# Revit family: HARMANN-SENSOVENT ROOF V EC-Wywiewny
name_source: partatom
category: Wyposażenie mechaniczne
units: mm (PartAtom-declared; Revit-internal decimal feet)

## family parameters
Oparty na płaszczyźnie roboczej = Nie
Punkt obliczania pomieszczeń = Nie
Tnij formami wycięć po wczytaniu = Nie
Typ części = Normalny
Współdzielony = Nie
Wymiar okrągłego złącza = Użyj średnicy
Zachowaj orientację opisów = Nie
Zawsze pionowo = Tak

## types (7) — shared parameters
Domyślna rzędna = 0.0 mm
IfcExportAs = IfcFanType
IfcExportType = NOTDEFINED
Kod Producent = Harmann
Kod Typoszereg = SENSOVENT ROOF V EC
Object Date = 2018.11.30
Object Destination = PL
Object ID = F000104RFAPL
Object Language = PL
Object Revit = 2017
Object Version = 1.00
Opis = Wentylator dachowy
Opt Akcesorium Podstawa A = ᴬ : Brak Podstawy
Opt Akcesorium Podstawa B = ᴬ : Podstawa Dachowa
Opt Akcesorium Podstawa C = ᴬ : Tłumiąca Podstawa Dachowa
Producent = Harmann Polska Sp. z o.o.
Producent Nazwa = Harmann Polska Sp. z o.o.
Systematyka Branża = Instalacje Sanitarne
Systematyka Dziedzina = Instalacje Wentylacyjne
Systematyka Klasa = Wentylator
Systematyka Rodzaj = Wentylator Dachowy
Zasilanie Częstotliwość Nominalna = 50 Hz
Zasilanie Ilość Faz = 1
Zasilanie Konfiguracja Uzwojeń = n/d
Zasilanie Napięcie Nominalne = 230 V
Zasilanie Rodzaj Sterowania = Sterowanie napięciem 0-10V
l1_a0 = 0.0 mm
l1_a1 = 0.0 mm
l1_a2 = 0.0 mm
l1_a3 = 0.0 mm
l1_a4 = 0.0 mm
l1_a5 = 320.0 mm
l1_a6 = 620.0 mm
l2_a0 = 0.0 mm
l2_a1 = 1.0 mm
l2_a4 = 1.0 mm
l2_a5 = 0.0 mm
l2_a6 = 0.0 mm
wz_a0 = 0.0 mm

## per-type parameters (varying)
- SENSOVENT ROOF V190 EC: Kod Numer Katalogowy=05002052; Masa Netto=4.5 kg; Opis indeksowy=SENSOVENT ROOF V190 EC; Otoczenie Poziom Ciśnienia Akustycznego Nominalny z 01 m=50; Otoczenie Poziom Ciśnienia Akustycznego Nominalny z 04 m=38; Otoczenie Poziom Ciśnienia Akustycznego Nominalny z 10 m=30; Otoczenie Poziom Mocy Akustycznej Nominalny Obudowa=61; Otoczenie Temperatura Maksymalna=60.0 °C; Otoczenie Temperatura Minimalna=-30.0 °C; Powietrze Wywiewane Ciśnienie Statyczne Maksymalne=670.0 Pa; Powietrze Wywiewane Ciśnienie Statyczne Nominalne=100.0 Pa; Powietrze Wywiewane Poziom Mocy Akustycznej Nominalny Wlot=60; Powietrze Wywiewane Przepływ Maksymalny=610 m³/h; Powietrze Wywiewane Przepływ Nominalny=250 m³/h; Powietrze Wywiewane Temperatura Maksymalna=60.0 °C; Prt Komponent A1=VE-Zagnieżdżone-Akcesorium-ParaForma-Harmann-DAF-Króciec_Przyłączeniowy : DAF 180; Prt Komponent A2=VE-Zagnieżdżone-Akcesorium-ParaForma-Harmann-DAS-Złącze_Przeciwdrganiowe : 180; Prt Komponent A3=VE-Zagnieżdżone-Akcesorium-ParaForma-Harmann-DVK-Przepustnica_Zwrotna : 180; Prt Komponent A4=VE-Zagnieżdżone-Akcesorium-ParaForma-Harmann-DKP-Płyta_Adaptacyjna : 220; Prt Komponent A5=VE-Zagnieżdżone-Akcesorium-ParaForma-Harmann-DSF_AL-Podstawa_Dachowa : 220; Prt Komponent A6=VE-Zagnieżdżone-Akcesorium-ParaForma-Harmann-DSS_AL-Podstawa_Dachowa : 220; Prt Komponent N1=GE-Komponent-ParaForma-Harmann-VIVER_EC-N1a : 2-190/600EC; Zasilanie Moc=114 W; Zasilanie Moc Pozorna=191 VA; Zasilanie Natężenie=1 A; Zasilanie Współczynnik Mocy=0.519; dn=180.0 mm; ds=220.0 mm; l2_a2=155.0 mm; l2_a3=115.0 mm; s1=180.0 mm; wx_a0=95.5 mm; wy_a0=95.5 mm
- SENSOVENT ROOF V220 EC: Kod Numer Katalogowy=05002053
05002053; Masa Netto=4.9 kg; Opis indeksowy=SENSOVENT ROOF V220 EC; Otoczenie Poziom Ciśnienia Akustycznego Nominalny z 01 m=45; Otoczenie Poziom Ciśnienia Akustycznego Nominalny z 04 m=33; Otoczenie Poziom Ciśnienia Akustycznego Nominalny z 10 m=25; Otoczenie Poziom Mocy Akustycznej Nominalny Obudowa=56; Otoczenie Temperatura Maksymalna=60.0 °C; Otoczenie Temperatura Minimalna=-30.0 °C; Powietrze Wywiewane Ciśnienie Statyczne Maksymalne=570.0 Pa; Powietrze Wywiewane Ciśnienie Statyczne Nominalne=100.0 Pa; Powietrze Wywiewane Poziom Mocy Akustycznej Nominalny Wlot=55; Powietrze Wywiewane Przepływ Maksymalny=940 m³/h; Powietrze Wywiewane Przepływ Nominalny=350 m³/h; Powietrze Wywiewane Temperatura Maksymalna=60.0 °C; Prt Komponent A1=VE-Zagnieżdżone-Akcesorium-ParaForma-Harmann-DAF-Króciec_Przyłączeniowy : DAF 180; Prt Komponent A2=VE-Zagnieżdżone-Akcesorium-ParaForma-Harmann-DAS-Złącze_Przeciwdrganiowe : 180; Prt Komponent A3=VE-Zagnieżdżone-Akcesorium-ParaForma-Harmann-DVK-Przepustnica_Zwrotna : 180; Prt Komponent A4=VE-Zagnieżdżone-Akcesorium-ParaForma-Harmann-DKP-Płyta_Adaptacyjna : 220; Prt Komponent A5=VE-Zagnieżdżone-Akcesorium-ParaForma-Harmann-DSF_AL-Podstawa_Dachowa : 220; Prt Komponent A6=VE-Zagnieżdżone-Akcesorium-ParaForma-Harmann-DSS_AL-Podstawa_Dachowa : 220; Prt Komponent N1=GE-Komponent-ParaForma-Harmann-VIVER_EC-N1a : 2-220/950EC; Zasilanie Moc=113 W; Zasilanie Moc Pozorna=214 VA; Zasilanie Natężenie=1 A; Zasilanie Współczynnik Mocy=0.528; dn=180.0 mm; ds=220.0 mm; l2_a2=155.0 mm; l2_a3=115.0 mm; s1=180.0 mm; wx_a0=95.5 mm; wy_a0=95.5 mm
- SENSOVENT ROOF V250 EC: Kod Numer Katalogowy=05002054; Masa Netto=6.5 kg; Object URL=http://www.paraforma.pl; Opis indeksowy=SENSOVENT ROOF V250 EC; Otoczenie Poziom Ciśnienia Akustycznego Nominalny z 01 m=50; Otoczenie Poziom Ciśnienia Akustycznego Nominalny z 04 m=38; Otoczenie Poziom Ciśnienia Akustycznego Nominalny z 10 m=30; Otoczenie Poziom Mocy Akustycznej Nominalny Obudowa=61; Otoczenie Temperatura Maksymalna=70.0 °C; Otoczenie Temperatura Minimalna=-30.0 °C; Powietrze Wywiewane Ciśnienie Statyczne Maksymalne=570.0 Pa; Powietrze Wywiewane Ciśnienie Statyczne Nominalne=100.0 Pa; Powietrze Wywiewane Poziom Mocy Akustycznej Nominalny Wlot=59; Powietrze Wywiewane Przepływ Maksymalny=1200 m³/h; Powietrze Wywiewane Przepływ Nominalny=450 m³/h; Powietrze Wywiewane Temperatura Maksymalna=70.0 °C; Prt Komponent A1=VE-Zagnieżdżone-Akcesorium-ParaForma-Harmann-DAF-Króciec_Przyłączeniowy : DAF 180; Prt Komponent A2=VE-Zagnieżdżone-Akcesorium-ParaForma-Harmann-DAS-Złącze_Przeciwdrganiowe : 180; Prt Komponent A3=VE-Zagnieżdżone-Akcesorium-ParaForma-Harmann-DVK-Przepustnica_Zwrotna : 180; Prt Komponent A4=VE-Zagnieżdżone-Akcesorium-ParaForma-Harmann-DKP-Płyta_Adaptacyjna : 220; Prt Komponent A5=VE-Zagnieżdżone-Akcesorium-ParaForma-Harmann-DSF_AL-Podstawa_Dachowa : 220; Prt Komponent A6=VE-Zagnieżdżone-Akcesorium-ParaForma-Harmann-DSS_AL-Podstawa_Dachowa : 220; Prt Komponent N1=GE-Komponent-ParaForma-Harmann-VIVER_EC-N1a : 2-250/1200EC; Zasilanie Moc=179 W; Zasilanie Moc Pozorna=345 VA; Zasilanie Natężenie=2 A; Zasilanie Współczynnik Mocy=0.519; dn=180.0 mm; ds=220.0 mm; l2_a2=155.0 mm; l2_a3=115.0 mm; s1=180.0 mm; wx_a0=95.5 mm; wy_a0=95.5 mm
- SENSOVENT ROOF V280 EC: Kod Numer Katalogowy=05002055; Masa Netto=8.0 kg; Opis indeksowy=SENSOVENT ROOF V280 EC; Otoczenie Poziom Ciśnienia Akustycznego Nominalny z 01 m=51; Otoczenie Poziom Ciśnienia Akustycznego Nominalny z 04 m=38; Otoczenie Poziom Ciśnienia Akustycznego Nominalny z 10 m=31; Otoczenie Poziom Mocy Akustycznej Nominalny Obudowa=62; Otoczenie Temperatura Maksymalna=55.0 °C; Otoczenie Temperatura Minimalna=-30.0 °C; Powietrze Wywiewane Ciśnienie Statyczne Maksymalne=830.0 Pa; Powietrze Wywiewane Ciśnienie Statyczne Nominalne=100.0 Pa; Powietrze Wywiewane Poziom Mocy Akustycznej Nominalny Wlot=62; Powietrze Wywiewane Przepływ Maksymalny=1970 m³/h; Powietrze Wywiewane Przepływ Nominalny=700 m³/h; Powietrze Wywiewane Temperatura Maksymalna=55.0 °C; Prt Komponent A1=VE-Zagnieżdżone-Akcesorium-ParaForma-Harmann-DAF-Króciec_Przyłączeniowy : DAF 250; Prt Komponent A2=VE-Zagnieżdżone-Akcesorium-ParaForma-Harmann-DAS-Złącze_Przeciwdrganiowe : 250; Prt Komponent A3=VE-Zagnieżdżone-Akcesorium-ParaForma-Harmann-DVK-Przepustnica_Zwrotna : 250; Prt Komponent A4=VE-Zagnieżdżone-Akcesorium-ParaForma-Harmann-DKP-Płyta_Adaptacyjna : 280; Prt Komponent A5=VE-Zagnieżdżone-Akcesorium-ParaForma-Harmann-DSF_AL-Podstawa_Dachowa : 280; Prt Komponent A6=VE-Zagnieżdżone-Akcesorium-ParaForma-Harmann-DSS_AL-Podstawa_Dachowa : 280; Prt Komponent N1=GE-Komponent-ParaForma-Harmann-VIVER_EC-N1a : 2-280/1900EC; Zasilanie Moc=268 W; Zasilanie Moc Pozorna=432 VA; Zasilanie Natężenie=2 A; Zasilanie Współczynnik Mocy=0.62; dn=250.0 mm; ds=280.0 mm; l2_a2=157.0 mm; l2_a3=156.0 mm; s1=250.0 mm; wx_a0=135.0 mm; wy_a0=135.0 mm
- SENSOVENT ROOF V350 EC: Kod Numer Katalogowy=05002056; Masa Netto=14.7 kg; Opis indeksowy=SENSOVENT ROOF V350 EC; Otoczenie Poziom Ciśnienia Akustycznego Nominalny z 01 m=46; Otoczenie Poziom Ciśnienia Akustycznego Nominalny z 04 m=34; Otoczenie Poziom Ciśnienia Akustycznego Nominalny z 10 m=26; Otoczenie Poziom Mocy Akustycznej Nominalny Obudowa=57; Otoczenie Temperatura Maksymalna=60.0 °C; Otoczenie Temperatura Minimalna=-25.0 °C; Powietrze Wywiewane Ciśnienie Statyczne Maksymalne=450.0 Pa; Powietrze Wywiewane Ciśnienie Statyczne Nominalne=100.0 Pa; Powietrze Wywiewane Poziom Mocy Akustycznej Nominalny Wlot=56; Powietrze Wywiewane Przepływ Maksymalny=2750 m³/h; Powietrze Wywiewane Przepływ Nominalny=1000 m³/h; Powietrze Wywiewane Temperatura Maksymalna=60.0 °C; Prt Komponent A1=VE-Zagnieżdżone-Akcesorium-ParaForma-Harmann-DAF-Króciec_Przyłączeniowy : DAF 400; Prt Komponent A2=VE-Zagnieżdżone-Akcesorium-ParaForma-Harmann-DAS-Złącze_Przeciwdrganiowe : 400; Prt Komponent A3=VE-Zagnieżdżone-Akcesorium-ParaForma-Harmann-DVK-Przepustnica_Zwrotna : 400; Prt Komponent A4=VE-Zagnieżdżone-Akcesorium-ParaForma-Harmann-DKP-Płyta_Adaptacyjna : 355; Prt Komponent A5=VE-Zagnieżdżone-Akcesorium-ParaForma-Harmann-DSF_AL-Podstawa_Dachowa : 355; Prt Komponent A6=VE-Zagnieżdżone-Akcesorium-ParaForma-Harmann-DSS_AL-Podstawa_Dachowa : 355; Prt Komponent N1=GE-Komponent-ParaForma-Harmann-VIVER_EC-N1a : 4-355/2700EC; Zasilanie Moc=165 W; Zasilanie Moc Pozorna=322 VA; Zasilanie Natężenie=1 A; Zasilanie Współczynnik Mocy=0.512; dn=400.0 mm; ds=355.0 mm; l2_a2=155.0 mm; l2_a3=220.0 mm; s1=400.0 mm; wx_a0=192.3 mm; wy_a0=192.5 mm
- SENSOVENT ROOF V400 EC: Kod Numer Katalogowy=05002057; Masa Netto=18.8 kg; Opis indeksowy=SENSOVENT ROOF V400 EC; Otoczenie Poziom Ciśnienia Akustycznego Nominalny z 01 m=48; Otoczenie Poziom Ciśnienia Akustycznego Nominalny z 04 m=36; Otoczenie Poziom Ciśnienia Akustycznego Nominalny z 10 m=28; Otoczenie Poziom Mocy Akustycznej Nominalny Obudowa=59; Otoczenie Temperatura Maksymalna=50.0 °C; Otoczenie Temperatura Minimalna=-25.0 °C; Powietrze Wywiewane Ciśnienie Statyczne Maksymalne=920.0 Pa; Powietrze Wywiewane Ciśnienie Statyczne Nominalne=150.0 Pa; Powietrze Wywiewane Poziom Mocy Akustycznej Nominalny Wlot=56; Powietrze Wywiewane Przepływ Maksymalny=4460 m³/h; Powietrze Wywiewane Przepływ Nominalny=1500 m³/h; Powietrze Wywiewane Temperatura Maksymalna=50.0 °C; Prt Komponent A1=VE-Zagnieżdżone-Akcesorium-ParaForma-Harmann-DAF-Króciec_Przyłączeniowy : DAF 400; Prt Komponent A2=VE-Zagnieżdżone-Akcesorium-ParaForma-Harmann-DAS-Złącze_Przeciwdrganiowe : 400; Prt Komponent A3=VE-Zagnieżdżone-Akcesorium-ParaForma-Harmann-DVK-Przepustnica_Zwrotna : 400; Prt Komponent A4=VE-Zagnieżdżone-Akcesorium-ParaForma-Harmann-DKP-Płyta_Adaptacyjna : 355; Prt Komponent A5=VE-Zagnieżdżone-Akcesorium-ParaForma-Harmann-DSF_AL-Podstawa_Dachowa : 355; Prt Komponent A6=VE-Zagnieżdżone-Akcesorium-ParaForma-Harmann-DSS_AL-Podstawa_Dachowa : 355; Prt Komponent N1=GE-Komponent-ParaForma-Harmann-VIVER_EC-N1a : 4-400/4400EC; Zasilanie Moc=503 W; Zasilanie Moc Pozorna=534 VA; Zasilanie Natężenie=2 A; Zasilanie Współczynnik Mocy=0.943; dn=400.0 mm; ds=355.0 mm; l2_a2=155.0 mm; l2_a3=220.0 mm; s1=400.0 mm; wx_a0=192.8 mm; wy_a0=192.5 mm
- SENSOVENT ROOF V450 EC: Kod Numer Katalogowy=05002058; Masa Netto=21.2 kg; Opis indeksowy=SENSOVENT ROOF V450 EC
SENSOVENT ROOF V450 EC; Otoczenie Poziom Ciśnienia Akustycznego Nominalny z 01 m=50; Otoczenie Poziom Ciśnienia Akustycznego Nominalny z 04 m=38; Otoczenie Poziom Ciśnienia Akustycznego Nominalny z 10 m=30; Otoczenie Poziom Mocy Akustycznej Nominalny Obudowa=61; Otoczenie Temperatura Maksymalna=50.0 °C; Otoczenie Temperatura Minimalna=-25.0 °C; Powietrze Wywiewane Ciśnienie Statyczne Maksymalne=640.0 Pa; Powietrze Wywiewane Ciśnienie Statyczne Nominalne=150.0 Pa; Powietrze Wywiewane Poziom Mocy Akustycznej Nominalny Wlot=60; Powietrze Wywiewane Przepływ Maksymalny=5550 m³/h; Powietrze Wywiewane Przepływ Nominalny=2000 m³/h; Powietrze Wywiewane Temperatura Maksymalna=50.0 °C; Prt Komponent A1=VE-Zagnieżdżone-Akcesorium-ParaForma-Harmann-DAF-Króciec_Przyłączeniowy : DAF 400; Prt Komponent A2=VE-Zagnieżdżone-Akcesorium-ParaForma-Harmann-DAS-Złącze_Przeciwdrganiowe : 400; Prt Komponent A3=VE-Zagnieżdżone-Akcesorium-ParaForma-Harmann-DVK-Przepustnica_Zwrotna : 400; Prt Komponent A4=VE-Zagnieżdżone-Akcesorium-ParaForma-Harmann-DKP-Płyta_Adaptacyjna : 450; Prt Komponent A5=VE-Zagnieżdżone-Akcesorium-ParaForma-Harmann-DSF_AL-Podstawa_Dachowa : 450; Prt Komponent A6=VE-Zagnieżdżone-Akcesorium-ParaForma-Harmann-DSS_AL-Podstawa_Dachowa : 450; Prt Komponent N1=GE-Komponent-ParaForma-Harmann-VIVER_EC-N1a : 4-450/5500EC; Zasilanie Moc=509 W; Zasilanie Moc Pozorna=538 VA; Zasilanie Natężenie=2 A; Zasilanie Współczynnik Mocy=0.946; dn=400.0 mm; ds=450.0 mm; l2_a2=155.0 mm; l2_a3=220.0 mm; s1=400.0 mm; wx_a0=220.0 mm; wy_a0=220.0 mm

note: column(s) folded — value = type name in every type: Kod Zamówienia, Model
